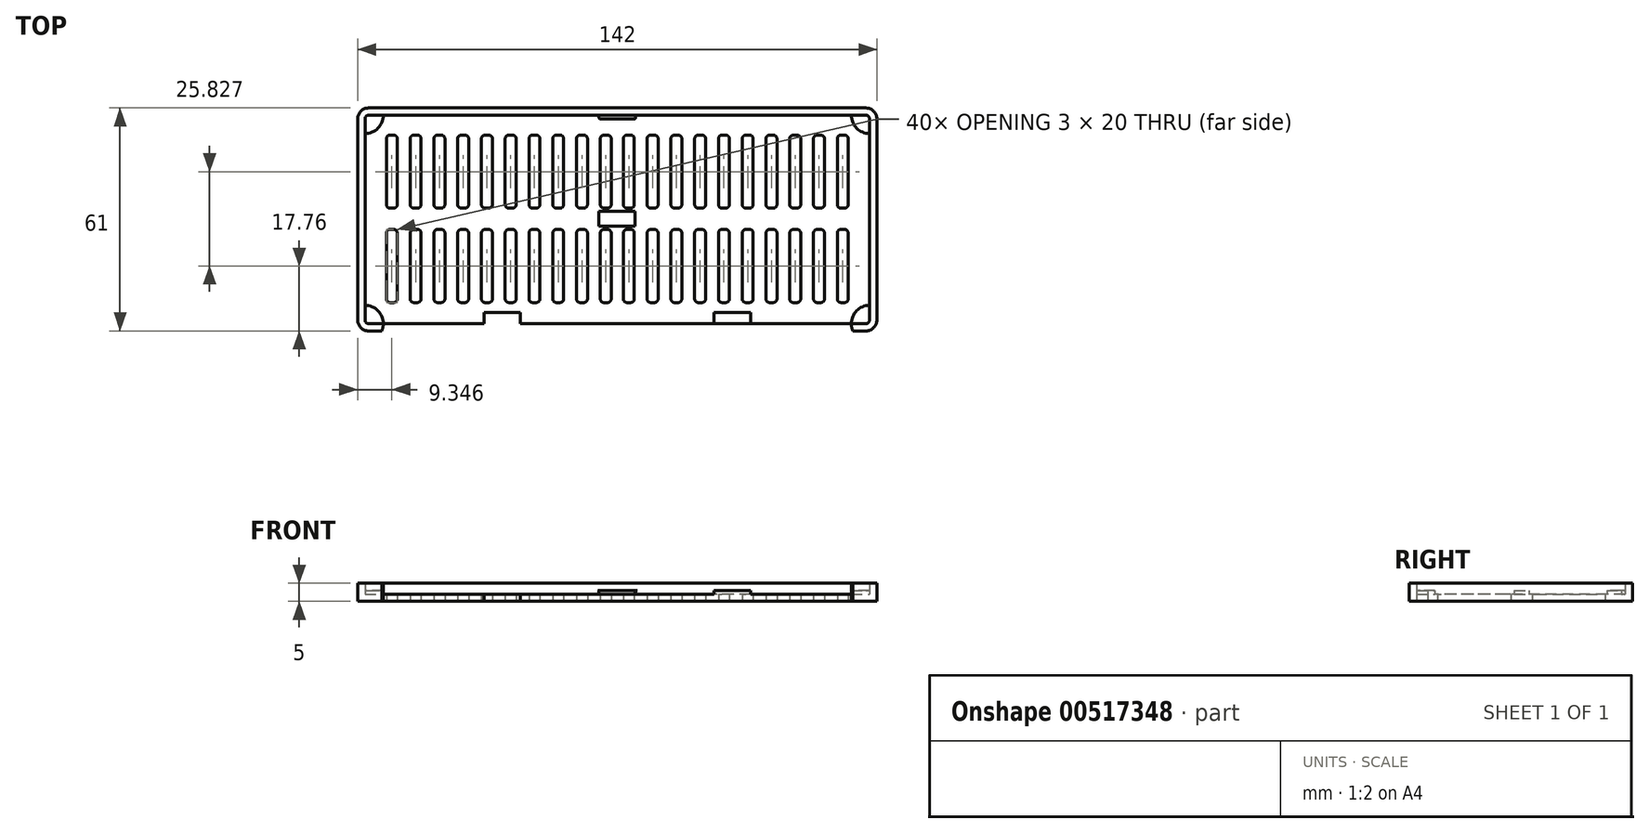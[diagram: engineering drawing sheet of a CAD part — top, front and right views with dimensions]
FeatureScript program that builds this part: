
annotation { "Feature Type Name" : "Feature", "Feature Type Description" : "" }
export const myFeature = defineFeature(function(context is Context, id is Id, definition is map)
    precondition{}
    {
        {
            var Q0;
            Q0=qCreatedBy(makeId("Top.planeOp"),FACE);
            var sketch = newSketch(context, id + "F0", { "sketchPlane" : qUnion([Q0])});
            skLineSegment(sketch, "E0.top", {"start": v(1, -57) * mm, "end": v(137, -57) * mm});
            skLineSegment(sketch, "E0.left", {"start": v(0, -1) * mm, "end": v(0, -56) * mm});
            skLineSegment(sketch, "E0.right", {"start": v(138, -1) * mm, "end": v(138, -56) * mm});
            skPoint(sketch, "E1.visualSharp", {"position": v(0, 0) * mm});
            skArc(sketch, "E1.filletArc", {"start": v(1, 0) * mm, "mid": v(0.3, -0.3) * mm, "end": v(0, -1) * mm});
            skPoint(sketch, "E2.visualSharp", {"position": v(0, -57) * mm});
            skArc(sketch, "E2.filletArc", {"start": v(0, -56) * mm, "mid": v(0.3, -56.7) * mm, "end": v(1, -57) * mm});
            skPoint(sketch, "E3.visualSharp", {"position": v(138, -57) * mm});
            skArc(sketch, "E3.filletArc", {"start": v(137, -57) * mm, "mid": v(137.7, -56.7) * mm, "end": v(138, -56) * mm});
            skPoint(sketch, "E4.visualSharp", {"position": v(138, 0) * mm});
            skArc(sketch, "E4.filletArc", {"start": v(138, -1) * mm, "mid": v(137.7, -0.3) * mm, "end": v(137, 0) * mm});
            skArc(sketch, "E5.0", {"start": v(1, 2) * mm, "mid": v(-1.12, 1.12) * mm, "end": v(-2, -1) * mm});
            skLineSegment(sketch, "E5.1", {"start": v(-2, -1) * mm, "end": v(-2, -56) * mm});
            skLineSegment(sketch, "E5.2", {"start": v(1, 2) * mm, "end": v(137, 2) * mm});
            skArc(sketch, "E5.3", {"start": v(-2, -56) * mm, "mid": v(-1.12, -58.12) * mm, "end": v(1, -59) * mm});
            skArc(sketch, "E5.4", {"start": v(140, -1) * mm, "mid": v(139.12, 1.12) * mm, "end": v(137, 2) * mm});
            skLineSegment(sketch, "E5.5", {"start": v(140, -1) * mm, "end": v(140, -56) * mm});
            skArc(sketch, "E5.6", {"start": v(137, -59) * mm, "mid": v(139.12, -58.12) * mm, "end": v(140, -56) * mm});
            skLineSegment(sketch, "E5.7", {"start": v(1, -59) * mm, "end": v(137, -59) * mm});
            skCircle(sketch, "E6", {"center": v(0, 0) * mm, "radius": 5 * mm});
            skCircle(sketch, "E7", {"center": v(0, -57) * mm, "radius": 5 * mm});
            skCircle(sketch, "E8", {"center": v(138, -57) * mm, "radius": 5 * mm});
            skCircle(sketch, "E9", {"center": v(138, 0) * mm, "radius": 5 * mm});
            skLineSegment(sketch, "E10.top", {"start": v(69, -1) * mm, "end": v(73.64, -1) * mm});
            skLineSegment(sketch, "E10.left", {"start": v(69, 0) * mm, "end": v(69, -1) * mm, "construction": true});
            skLineSegment(sketch, "E10.right", {"start": v(74, -0.43) * mm, "end": v(74, -0.64) * mm});
            skLineSegment(sketch, "E11.MirrorCS", {"start": v(69, -1) * mm, "end": v(64.36, -1) * mm});
            skLineSegment(sketch, "E12.MirrorCS", {"start": v(64, -0.36) * mm, "end": v(64, -0.64) * mm});
            skLineSegment(sketch, "E13.bottom", {"start": v(32.53, -57) * mm, "end": v(42.53, -57) * mm});
            skLineSegment(sketch, "E13.top", {"start": v(32.53, -54) * mm, "end": v(42.53, -54) * mm});
            skLineSegment(sketch, "E13.left", {"start": v(32.53, -57) * mm, "end": v(32.53, -54) * mm});
            skLineSegment(sketch, "E13.right", {"start": v(42.53, -57) * mm, "end": v(42.53, -54) * mm});
            skLineSegment(sketch, "E14.MirrorCS", {"start": v(95.47, -57) * mm, "end": v(95.47, -54) * mm});
            skLineSegment(sketch, "E15.MirrorCS", {"start": v(105.47, -54) * mm, "end": v(95.47, -54) * mm});
            skLineSegment(sketch, "E16.MirrorCS", {"start": v(105.47, -57) * mm, "end": v(105.47, -54) * mm});
            skLineSegment(sketch, "E17", {"start": v(0, -28.5) * mm, "end": v(138, -28.5) * mm, "construction": true});
            skLineSegment(sketch, "E18.top", {"start": v(6.85, -5.41) * mm, "end": v(7.85, -5.41) * mm});
            skLineSegment(sketch, "E18.left", {"start": v(5.85, -24.41) * mm, "end": v(5.85, -6.41) * mm});
            skLineSegment(sketch, "E18.right", {"start": v(8.85, -24.41) * mm, "end": v(8.85, -6.41) * mm});
            skPoint(sketch, "E19.visualSharp", {"position": v(5.85, -5.41) * mm});
            skArc(sketch, "E19.filletArc", {"start": v(6.85, -5.41) * mm, "mid": v(6.14, -5.7) * mm, "end": v(5.85, -6.41) * mm});
            skPoint(sketch, "E20.visualSharp", {"position": v(8.85, -5.41) * mm});
            skArc(sketch, "E20.filletArc", {"start": v(8.85, -6.41) * mm, "mid": v(8.55, -5.7) * mm, "end": v(7.85, -5.41) * mm});
            skLineSegment(sketch, "E21.MirrorCS", {"start": v(-0.23, -28.33) * mm, "end": v(138, -28.33) * mm, "construction": true});
            skLineSegment(sketch, "E22.bottom", {"start": v(6.85, -25.41) * mm, "end": v(7.85, -25.41) * mm});
            skArc(sketch, "E23.filletArc", {"start": v(7.85, -25.41) * mm, "mid": v(8.55, -25.12) * mm, "end": v(8.85, -24.41) * mm});
            skArc(sketch, "E24.filletArc", {"start": v(5.85, -24.41) * mm, "mid": v(6.14, -25.12) * mm, "end": v(6.85, -25.41) * mm});
            skArc(sketch, "E25.MirrorCS", {"start": v(8.85, -50.24) * mm, "mid": v(8.55, -50.95) * mm, "end": v(7.85, -51.24) * mm});
            skArc(sketch, "E26.MirrorCS", {"start": v(6.85, -51.24) * mm, "mid": v(6.14, -50.95) * mm, "end": v(5.85, -50.24) * mm});
            skLineSegment(sketch, "E27.MirrorCS", {"start": v(6.85, -51.24) * mm, "end": v(7.85, -51.24) * mm});
            skLineSegment(sketch, "E28.MirrorCS", {"start": v(8.85, -32.24) * mm, "end": v(8.85, -50.24) * mm});
            skLineSegment(sketch, "E29.MirrorCS", {"start": v(6.85, -31.24) * mm, "end": v(7.85, -31.24) * mm});
            skLineSegment(sketch, "E30.MirrorCS", {"start": v(5.85, -32.24) * mm, "end": v(5.85, -50.24) * mm});
            skArc(sketch, "E31.MirrorCS", {"start": v(5.85, -32.24) * mm, "mid": v(6.14, -31.53) * mm, "end": v(6.85, -31.24) * mm});
            skArc(sketch, "E32.MirrorCS", {"start": v(7.85, -31.24) * mm, "mid": v(8.55, -31.53) * mm, "end": v(8.85, -32.24) * mm});
            skPoint(sketch, "E33.1.0.0", {"position": v(15.35, -5.41) * mm});
            skPoint(sketch, "E33.1.0.1", {"position": v(12.35, -5.41) * mm});
            skLineSegment(sketch, "E33.1.0.2", {"start": v(15.35, -24.41) * mm, "end": v(15.35, -6.41) * mm});
            skLineSegment(sketch, "E33.1.0.3", {"start": v(12.35, -24.41) * mm, "end": v(12.35, -6.41) * mm});
            skArc(sketch, "E33.1.0.4", {"start": v(12.35, -24.41) * mm, "mid": v(12.64, -25.12) * mm, "end": v(13.35, -25.41) * mm});
            skArc(sketch, "E33.1.0.5", {"start": v(15.35, -6.41) * mm, "mid": v(15.05, -5.7) * mm, "end": v(14.35, -5.41) * mm});
            skArc(sketch, "E33.1.0.6", {"start": v(13.35, -5.41) * mm, "mid": v(12.64, -5.7) * mm, "end": v(12.35, -6.41) * mm});
            skLineSegment(sketch, "E33.1.0.7", {"start": v(13.35, -25.41) * mm, "end": v(14.35, -25.41) * mm});
            skLineSegment(sketch, "E33.1.0.8", {"start": v(13.35, -5.41) * mm, "end": v(14.35, -5.41) * mm});
            skArc(sketch, "E33.1.0.9", {"start": v(14.35, -25.41) * mm, "mid": v(15.05, -25.12) * mm, "end": v(15.35, -24.41) * mm});
            skLineSegment(sketch, "E33.1.0.10", {"start": v(15.35, -32.24) * mm, "end": v(15.35, -50.24) * mm});
            skLineSegment(sketch, "E33.1.0.11", {"start": v(12.35, -32.24) * mm, "end": v(12.35, -50.24) * mm});
            skArc(sketch, "E33.1.0.12", {"start": v(15.35, -50.24) * mm, "mid": v(15.05, -50.95) * mm, "end": v(14.35, -51.24) * mm});
            skArc(sketch, "E33.1.0.13", {"start": v(14.35, -31.24) * mm, "mid": v(15.05, -31.53) * mm, "end": v(15.35, -32.24) * mm});
            skArc(sketch, "E33.1.0.14", {"start": v(12.35, -32.24) * mm, "mid": v(12.64, -31.53) * mm, "end": v(13.35, -31.24) * mm});
            skLineSegment(sketch, "E33.1.0.15", {"start": v(13.35, -31.24) * mm, "end": v(14.35, -31.24) * mm});
            skArc(sketch, "E33.1.0.16", {"start": v(13.35, -51.24) * mm, "mid": v(12.64, -50.95) * mm, "end": v(12.35, -50.24) * mm});
            skLineSegment(sketch, "E33.1.0.17", {"start": v(13.35, -51.24) * mm, "end": v(14.35, -51.24) * mm});
            skPoint(sketch, "E33.2.0.0", {"position": v(21.85, -5.41) * mm});
            skPoint(sketch, "E33.2.0.1", {"position": v(18.85, -5.41) * mm});
            skLineSegment(sketch, "E33.2.0.2", {"start": v(21.85, -24.41) * mm, "end": v(21.85, -6.41) * mm});
            skLineSegment(sketch, "E33.2.0.3", {"start": v(18.85, -24.41) * mm, "end": v(18.85, -6.41) * mm});
            skArc(sketch, "E33.2.0.4", {"start": v(18.85, -24.41) * mm, "mid": v(19.14, -25.12) * mm, "end": v(19.85, -25.41) * mm});
            skArc(sketch, "E33.2.0.5", {"start": v(21.85, -6.41) * mm, "mid": v(21.55, -5.7) * mm, "end": v(20.85, -5.41) * mm});
            skArc(sketch, "E33.2.0.6", {"start": v(19.85, -5.41) * mm, "mid": v(19.14, -5.7) * mm, "end": v(18.85, -6.41) * mm});
            skLineSegment(sketch, "E33.2.0.7", {"start": v(19.85, -25.41) * mm, "end": v(20.85, -25.41) * mm});
            skLineSegment(sketch, "E33.2.0.8", {"start": v(19.85, -5.41) * mm, "end": v(20.85, -5.41) * mm});
            skArc(sketch, "E33.2.0.9", {"start": v(20.85, -25.41) * mm, "mid": v(21.55, -25.12) * mm, "end": v(21.85, -24.41) * mm});
            skLineSegment(sketch, "E33.2.0.10", {"start": v(21.85, -32.24) * mm, "end": v(21.85, -50.24) * mm});
            skLineSegment(sketch, "E33.2.0.11", {"start": v(18.85, -32.24) * mm, "end": v(18.85, -50.24) * mm});
            skArc(sketch, "E33.2.0.12", {"start": v(21.85, -50.24) * mm, "mid": v(21.55, -50.95) * mm, "end": v(20.85, -51.24) * mm});
            skArc(sketch, "E33.2.0.13", {"start": v(20.85, -31.24) * mm, "mid": v(21.55, -31.53) * mm, "end": v(21.85, -32.24) * mm});
            skArc(sketch, "E33.2.0.14", {"start": v(18.85, -32.24) * mm, "mid": v(19.14, -31.53) * mm, "end": v(19.85, -31.24) * mm});
            skLineSegment(sketch, "E33.2.0.15", {"start": v(19.85, -31.24) * mm, "end": v(20.85, -31.24) * mm});
            skArc(sketch, "E33.2.0.16", {"start": v(19.85, -51.24) * mm, "mid": v(19.14, -50.95) * mm, "end": v(18.85, -50.24) * mm});
            skLineSegment(sketch, "E33.2.0.17", {"start": v(19.85, -51.24) * mm, "end": v(20.85, -51.24) * mm});
            skPoint(sketch, "E33.3.0.0", {"position": v(28.35, -5.41) * mm});
            skPoint(sketch, "E33.3.0.1", {"position": v(25.35, -5.41) * mm});
            skLineSegment(sketch, "E33.3.0.2", {"start": v(28.35, -24.41) * mm, "end": v(28.35, -6.41) * mm});
            skLineSegment(sketch, "E33.3.0.3", {"start": v(25.35, -24.41) * mm, "end": v(25.35, -6.41) * mm});
            skArc(sketch, "E33.3.0.4", {"start": v(25.35, -24.41) * mm, "mid": v(25.64, -25.12) * mm, "end": v(26.35, -25.41) * mm});
            skArc(sketch, "E33.3.0.5", {"start": v(28.35, -6.41) * mm, "mid": v(28.05, -5.7) * mm, "end": v(27.35, -5.41) * mm});
            skArc(sketch, "E33.3.0.6", {"start": v(26.35, -5.41) * mm, "mid": v(25.64, -5.7) * mm, "end": v(25.35, -6.41) * mm});
            skLineSegment(sketch, "E33.3.0.7", {"start": v(26.35, -25.41) * mm, "end": v(27.35, -25.41) * mm});
            skLineSegment(sketch, "E33.3.0.8", {"start": v(26.35, -5.41) * mm, "end": v(27.35, -5.41) * mm});
            skArc(sketch, "E33.3.0.9", {"start": v(27.35, -25.41) * mm, "mid": v(28.05, -25.12) * mm, "end": v(28.35, -24.41) * mm});
            skLineSegment(sketch, "E33.3.0.10", {"start": v(28.35, -32.24) * mm, "end": v(28.35, -50.24) * mm});
            skLineSegment(sketch, "E33.3.0.11", {"start": v(25.35, -32.24) * mm, "end": v(25.35, -50.24) * mm});
            skArc(sketch, "E33.3.0.12", {"start": v(28.35, -50.24) * mm, "mid": v(28.05, -50.95) * mm, "end": v(27.35, -51.24) * mm});
            skArc(sketch, "E33.3.0.13", {"start": v(27.35, -31.24) * mm, "mid": v(28.05, -31.53) * mm, "end": v(28.35, -32.24) * mm});
            skArc(sketch, "E33.3.0.14", {"start": v(25.35, -32.24) * mm, "mid": v(25.64, -31.53) * mm, "end": v(26.35, -31.24) * mm});
            skLineSegment(sketch, "E33.3.0.15", {"start": v(26.35, -31.24) * mm, "end": v(27.35, -31.24) * mm});
            skArc(sketch, "E33.3.0.16", {"start": v(26.35, -51.24) * mm, "mid": v(25.64, -50.95) * mm, "end": v(25.35, -50.24) * mm});
            skLineSegment(sketch, "E33.3.0.17", {"start": v(26.35, -51.24) * mm, "end": v(27.35, -51.24) * mm});
            skPoint(sketch, "E33.4.0.0", {"position": v(34.85, -5.41) * mm});
            skPoint(sketch, "E33.4.0.1", {"position": v(31.85, -5.41) * mm});
            skLineSegment(sketch, "E33.4.0.2", {"start": v(34.85, -24.41) * mm, "end": v(34.85, -6.41) * mm});
            skLineSegment(sketch, "E33.4.0.3", {"start": v(31.85, -24.41) * mm, "end": v(31.85, -6.41) * mm});
            skArc(sketch, "E33.4.0.4", {"start": v(31.85, -24.41) * mm, "mid": v(32.14, -25.12) * mm, "end": v(32.85, -25.41) * mm});
            skArc(sketch, "E33.4.0.5", {"start": v(34.85, -6.41) * mm, "mid": v(34.55, -5.7) * mm, "end": v(33.85, -5.41) * mm});
            skArc(sketch, "E33.4.0.6", {"start": v(32.85, -5.41) * mm, "mid": v(32.14, -5.7) * mm, "end": v(31.85, -6.41) * mm});
            skLineSegment(sketch, "E33.4.0.7", {"start": v(32.85, -25.41) * mm, "end": v(33.85, -25.41) * mm});
            skLineSegment(sketch, "E33.4.0.8", {"start": v(32.85, -5.41) * mm, "end": v(33.85, -5.41) * mm});
            skArc(sketch, "E33.4.0.9", {"start": v(33.85, -25.41) * mm, "mid": v(34.55, -25.12) * mm, "end": v(34.85, -24.41) * mm});
            skLineSegment(sketch, "E33.4.0.10", {"start": v(34.85, -32.24) * mm, "end": v(34.85, -50.24) * mm});
            skLineSegment(sketch, "E33.4.0.11", {"start": v(31.85, -32.24) * mm, "end": v(31.85, -50.24) * mm});
            skArc(sketch, "E33.4.0.12", {"start": v(34.85, -50.24) * mm, "mid": v(34.55, -50.95) * mm, "end": v(33.85, -51.24) * mm});
            skArc(sketch, "E33.4.0.13", {"start": v(33.85, -31.24) * mm, "mid": v(34.55, -31.53) * mm, "end": v(34.85, -32.24) * mm});
            skArc(sketch, "E33.4.0.14", {"start": v(31.85, -32.24) * mm, "mid": v(32.14, -31.53) * mm, "end": v(32.85, -31.24) * mm});
            skLineSegment(sketch, "E33.4.0.15", {"start": v(32.85, -31.24) * mm, "end": v(33.85, -31.24) * mm});
            skArc(sketch, "E33.4.0.16", {"start": v(32.85, -51.24) * mm, "mid": v(32.14, -50.95) * mm, "end": v(31.85, -50.24) * mm});
            skLineSegment(sketch, "E33.4.0.17", {"start": v(32.85, -51.24) * mm, "end": v(33.85, -51.24) * mm});
            skPoint(sketch, "E33.5.0.0", {"position": v(41.35, -5.41) * mm});
            skPoint(sketch, "E33.5.0.1", {"position": v(38.35, -5.41) * mm});
            skLineSegment(sketch, "E33.5.0.2", {"start": v(41.35, -24.41) * mm, "end": v(41.35, -6.41) * mm});
            skLineSegment(sketch, "E33.5.0.3", {"start": v(38.35, -24.41) * mm, "end": v(38.35, -6.41) * mm});
            skArc(sketch, "E33.5.0.4", {"start": v(38.35, -24.41) * mm, "mid": v(38.64, -25.12) * mm, "end": v(39.35, -25.41) * mm});
            skArc(sketch, "E33.5.0.5", {"start": v(41.35, -6.41) * mm, "mid": v(41.05, -5.7) * mm, "end": v(40.35, -5.41) * mm});
            skArc(sketch, "E33.5.0.6", {"start": v(39.35, -5.41) * mm, "mid": v(38.64, -5.7) * mm, "end": v(38.35, -6.41) * mm});
            skLineSegment(sketch, "E33.5.0.7", {"start": v(39.35, -25.41) * mm, "end": v(40.35, -25.41) * mm});
            skLineSegment(sketch, "E33.5.0.8", {"start": v(39.35, -5.41) * mm, "end": v(40.35, -5.41) * mm});
            skArc(sketch, "E33.5.0.9", {"start": v(40.35, -25.41) * mm, "mid": v(41.05, -25.12) * mm, "end": v(41.35, -24.41) * mm});
            skLineSegment(sketch, "E33.5.0.10", {"start": v(41.35, -32.24) * mm, "end": v(41.35, -50.24) * mm});
            skLineSegment(sketch, "E33.5.0.11", {"start": v(38.35, -32.24) * mm, "end": v(38.35, -50.24) * mm});
            skArc(sketch, "E33.5.0.12", {"start": v(41.35, -50.24) * mm, "mid": v(41.05, -50.95) * mm, "end": v(40.35, -51.24) * mm});
            skArc(sketch, "E33.5.0.13", {"start": v(40.35, -31.24) * mm, "mid": v(41.05, -31.53) * mm, "end": v(41.35, -32.24) * mm});
            skArc(sketch, "E33.5.0.14", {"start": v(38.35, -32.24) * mm, "mid": v(38.64, -31.53) * mm, "end": v(39.35, -31.24) * mm});
            skLineSegment(sketch, "E33.5.0.15", {"start": v(39.35, -31.24) * mm, "end": v(40.35, -31.24) * mm});
            skArc(sketch, "E33.5.0.16", {"start": v(39.35, -51.24) * mm, "mid": v(38.64, -50.95) * mm, "end": v(38.35, -50.24) * mm});
            skLineSegment(sketch, "E33.5.0.17", {"start": v(39.35, -51.24) * mm, "end": v(40.35, -51.24) * mm});
            skPoint(sketch, "E33.6.0.0", {"position": v(47.85, -5.41) * mm});
            skPoint(sketch, "E33.6.0.1", {"position": v(44.85, -5.41) * mm});
            skLineSegment(sketch, "E33.6.0.2", {"start": v(47.85, -24.41) * mm, "end": v(47.85, -6.41) * mm});
            skLineSegment(sketch, "E33.6.0.3", {"start": v(44.85, -24.41) * mm, "end": v(44.85, -6.41) * mm});
            skArc(sketch, "E33.6.0.4", {"start": v(44.85, -24.41) * mm, "mid": v(45.14, -25.12) * mm, "end": v(45.85, -25.41) * mm});
            skArc(sketch, "E33.6.0.5", {"start": v(47.85, -6.41) * mm, "mid": v(47.55, -5.7) * mm, "end": v(46.85, -5.41) * mm});
            skArc(sketch, "E33.6.0.6", {"start": v(45.85, -5.41) * mm, "mid": v(45.14, -5.7) * mm, "end": v(44.85, -6.41) * mm});
            skLineSegment(sketch, "E33.6.0.7", {"start": v(45.85, -25.41) * mm, "end": v(46.85, -25.41) * mm});
            skLineSegment(sketch, "E33.6.0.8", {"start": v(45.85, -5.41) * mm, "end": v(46.85, -5.41) * mm});
            skArc(sketch, "E33.6.0.9", {"start": v(46.85, -25.41) * mm, "mid": v(47.55, -25.12) * mm, "end": v(47.85, -24.41) * mm});
            skLineSegment(sketch, "E33.6.0.10", {"start": v(47.85, -32.24) * mm, "end": v(47.85, -50.24) * mm});
            skLineSegment(sketch, "E33.6.0.11", {"start": v(44.85, -32.24) * mm, "end": v(44.85, -50.24) * mm});
            skArc(sketch, "E33.6.0.12", {"start": v(47.85, -50.24) * mm, "mid": v(47.55, -50.95) * mm, "end": v(46.85, -51.24) * mm});
            skArc(sketch, "E33.6.0.13", {"start": v(46.85, -31.24) * mm, "mid": v(47.55, -31.53) * mm, "end": v(47.85, -32.24) * mm});
            skArc(sketch, "E33.6.0.14", {"start": v(44.85, -32.24) * mm, "mid": v(45.14, -31.53) * mm, "end": v(45.85, -31.24) * mm});
            skLineSegment(sketch, "E33.6.0.15", {"start": v(45.85, -31.24) * mm, "end": v(46.85, -31.24) * mm});
            skArc(sketch, "E33.6.0.16", {"start": v(45.85, -51.24) * mm, "mid": v(45.14, -50.95) * mm, "end": v(44.85, -50.24) * mm});
            skLineSegment(sketch, "E33.6.0.17", {"start": v(45.85, -51.24) * mm, "end": v(46.85, -51.24) * mm});
            skPoint(sketch, "E33.7.0.0", {"position": v(54.35, -5.41) * mm});
            skPoint(sketch, "E33.7.0.1", {"position": v(51.35, -5.41) * mm});
            skLineSegment(sketch, "E33.7.0.2", {"start": v(54.35, -24.41) * mm, "end": v(54.35, -6.41) * mm});
            skLineSegment(sketch, "E33.7.0.3", {"start": v(51.35, -24.41) * mm, "end": v(51.35, -6.41) * mm});
            skArc(sketch, "E33.7.0.4", {"start": v(51.35, -24.41) * mm, "mid": v(51.64, -25.12) * mm, "end": v(52.35, -25.41) * mm});
            skArc(sketch, "E33.7.0.5", {"start": v(54.35, -6.41) * mm, "mid": v(54.05, -5.7) * mm, "end": v(53.35, -5.41) * mm});
            skArc(sketch, "E33.7.0.6", {"start": v(52.35, -5.41) * mm, "mid": v(51.64, -5.7) * mm, "end": v(51.35, -6.41) * mm});
            skLineSegment(sketch, "E33.7.0.7", {"start": v(52.35, -25.41) * mm, "end": v(53.35, -25.41) * mm});
            skLineSegment(sketch, "E33.7.0.8", {"start": v(52.35, -5.41) * mm, "end": v(53.35, -5.41) * mm});
            skArc(sketch, "E33.7.0.9", {"start": v(53.35, -25.41) * mm, "mid": v(54.05, -25.12) * mm, "end": v(54.35, -24.41) * mm});
            skLineSegment(sketch, "E33.7.0.10", {"start": v(54.35, -32.24) * mm, "end": v(54.35, -50.24) * mm});
            skLineSegment(sketch, "E33.7.0.11", {"start": v(51.35, -32.24) * mm, "end": v(51.35, -50.24) * mm});
            skArc(sketch, "E33.7.0.12", {"start": v(54.35, -50.24) * mm, "mid": v(54.05, -50.95) * mm, "end": v(53.35, -51.24) * mm});
            skArc(sketch, "E33.7.0.13", {"start": v(53.35, -31.24) * mm, "mid": v(54.05, -31.53) * mm, "end": v(54.35, -32.24) * mm});
            skArc(sketch, "E33.7.0.14", {"start": v(51.35, -32.24) * mm, "mid": v(51.64, -31.53) * mm, "end": v(52.35, -31.24) * mm});
            skLineSegment(sketch, "E33.7.0.15", {"start": v(52.35, -31.24) * mm, "end": v(53.35, -31.24) * mm});
            skArc(sketch, "E33.7.0.16", {"start": v(52.35, -51.24) * mm, "mid": v(51.64, -50.95) * mm, "end": v(51.35, -50.24) * mm});
            skLineSegment(sketch, "E33.7.0.17", {"start": v(52.35, -51.24) * mm, "end": v(53.35, -51.24) * mm});
            skPoint(sketch, "E33.8.0.0", {"position": v(60.85, -5.41) * mm});
            skPoint(sketch, "E33.8.0.1", {"position": v(57.85, -5.41) * mm});
            skLineSegment(sketch, "E33.8.0.2", {"start": v(60.85, -24.41) * mm, "end": v(60.85, -6.41) * mm});
            skLineSegment(sketch, "E33.8.0.3", {"start": v(57.85, -24.41) * mm, "end": v(57.85, -6.41) * mm});
            skArc(sketch, "E33.8.0.4", {"start": v(57.85, -24.41) * mm, "mid": v(58.14, -25.12) * mm, "end": v(58.85, -25.41) * mm});
            skArc(sketch, "E33.8.0.5", {"start": v(60.85, -6.41) * mm, "mid": v(60.55, -5.7) * mm, "end": v(59.85, -5.41) * mm});
            skArc(sketch, "E33.8.0.6", {"start": v(58.85, -5.41) * mm, "mid": v(58.14, -5.7) * mm, "end": v(57.85, -6.41) * mm});
            skLineSegment(sketch, "E33.8.0.7", {"start": v(58.85, -25.41) * mm, "end": v(59.85, -25.41) * mm});
            skLineSegment(sketch, "E33.8.0.8", {"start": v(58.85, -5.41) * mm, "end": v(59.85, -5.41) * mm});
            skArc(sketch, "E33.8.0.9", {"start": v(59.85, -25.41) * mm, "mid": v(60.55, -25.12) * mm, "end": v(60.85, -24.41) * mm});
            skLineSegment(sketch, "E33.8.0.10", {"start": v(60.85, -32.24) * mm, "end": v(60.85, -50.24) * mm});
            skLineSegment(sketch, "E33.8.0.11", {"start": v(57.85, -32.24) * mm, "end": v(57.85, -50.24) * mm});
            skArc(sketch, "E33.8.0.12", {"start": v(60.85, -50.24) * mm, "mid": v(60.55, -50.95) * mm, "end": v(59.85, -51.24) * mm});
            skArc(sketch, "E33.8.0.13", {"start": v(59.85, -31.24) * mm, "mid": v(60.55, -31.53) * mm, "end": v(60.85, -32.24) * mm});
            skArc(sketch, "E33.8.0.14", {"start": v(57.85, -32.24) * mm, "mid": v(58.14, -31.53) * mm, "end": v(58.85, -31.24) * mm});
            skLineSegment(sketch, "E33.8.0.15", {"start": v(58.85, -31.24) * mm, "end": v(59.85, -31.24) * mm});
            skArc(sketch, "E33.8.0.16", {"start": v(58.85, -51.24) * mm, "mid": v(58.14, -50.95) * mm, "end": v(57.85, -50.24) * mm});
            skLineSegment(sketch, "E33.8.0.17", {"start": v(58.85, -51.24) * mm, "end": v(59.85, -51.24) * mm});
            skPoint(sketch, "E33.9.0.0", {"position": v(67.35, -5.41) * mm});
            skPoint(sketch, "E33.9.0.1", {"position": v(64.35, -5.41) * mm});
            skLineSegment(sketch, "E33.9.0.2", {"start": v(67.35, -24.41) * mm, "end": v(67.35, -6.41) * mm});
            skLineSegment(sketch, "E33.9.0.3", {"start": v(64.35, -24.41) * mm, "end": v(64.35, -6.41) * mm});
            skArc(sketch, "E33.9.0.4", {"start": v(64.35, -24.41) * mm, "mid": v(64.64, -25.12) * mm, "end": v(65.35, -25.41) * mm});
            skArc(sketch, "E33.9.0.5", {"start": v(67.35, -6.41) * mm, "mid": v(67.05, -5.7) * mm, "end": v(66.35, -5.41) * mm});
            skArc(sketch, "E33.9.0.6", {"start": v(65.35, -5.41) * mm, "mid": v(64.64, -5.7) * mm, "end": v(64.35, -6.41) * mm});
            skLineSegment(sketch, "E33.9.0.7", {"start": v(65.35, -25.41) * mm, "end": v(66.35, -25.41) * mm});
            skLineSegment(sketch, "E33.9.0.8", {"start": v(65.35, -5.41) * mm, "end": v(66.35, -5.41) * mm});
            skArc(sketch, "E33.9.0.9", {"start": v(66.35, -25.41) * mm, "mid": v(67.05, -25.12) * mm, "end": v(67.35, -24.41) * mm});
            skLineSegment(sketch, "E33.9.0.10", {"start": v(67.35, -32.24) * mm, "end": v(67.35, -50.24) * mm});
            skLineSegment(sketch, "E33.9.0.11", {"start": v(64.35, -32.24) * mm, "end": v(64.35, -50.24) * mm});
            skArc(sketch, "E33.9.0.12", {"start": v(67.35, -50.24) * mm, "mid": v(67.05, -50.95) * mm, "end": v(66.35, -51.24) * mm});
            skArc(sketch, "E33.9.0.13", {"start": v(66.35, -31.24) * mm, "mid": v(67.05, -31.53) * mm, "end": v(67.35, -32.24) * mm});
            skArc(sketch, "E33.9.0.14", {"start": v(64.35, -32.24) * mm, "mid": v(64.64, -31.53) * mm, "end": v(65.35, -31.24) * mm});
            skLineSegment(sketch, "E33.9.0.15", {"start": v(65.35, -31.24) * mm, "end": v(66.35, -31.24) * mm});
            skArc(sketch, "E33.9.0.16", {"start": v(65.35, -51.24) * mm, "mid": v(64.64, -50.95) * mm, "end": v(64.35, -50.24) * mm});
            skLineSegment(sketch, "E33.9.0.17", {"start": v(65.35, -51.24) * mm, "end": v(66.35, -51.24) * mm});
            skLineSegment(sketch, "E33.direction1", {"start": v(6.85, -25.41) * mm, "end": v(13.35, -25.41) * mm, "construction": true});
            skLineSegment(sketch, "E34", {"start": v(69, -57) * mm, "end": v(69, 2) * mm, "construction": true});
            skArc(sketch, "E35.MirrorCS", {"start": v(109.65, -6.41) * mm, "mid": v(109.95, -5.7) * mm, "end": v(110.65, -5.41) * mm});
            skArc(sketch, "E36.MirrorCS", {"start": v(118.15, -5.41) * mm, "mid": v(118.86, -5.7) * mm, "end": v(119.15, -6.41) * mm});
            skLineSegment(sketch, "E37.MirrorCS", {"start": v(131.15, -5.41) * mm, "end": v(130.15, -5.41) * mm});
            skLineSegment(sketch, "E38.MirrorCS", {"start": v(111.65, -5.41) * mm, "end": v(110.65, -5.41) * mm});
            skLineSegment(sketch, "E39.MirrorCS", {"start": v(92.15, -5.41) * mm, "end": v(91.15, -5.41) * mm});
            skLineSegment(sketch, "E40.MirrorCS", {"start": v(131.15, -25.41) * mm, "end": v(130.15, -25.41) * mm});
            skLineSegment(sketch, "E41.MirrorCS", {"start": v(124.65, -25.41) * mm, "end": v(123.65, -25.41) * mm});
            skLineSegment(sketch, "E42.MirrorCS", {"start": v(98.65, -5.41) * mm, "end": v(97.65, -5.41) * mm});
            skLineSegment(sketch, "E43.MirrorCS", {"start": v(118.15, -5.41) * mm, "end": v(117.15, -5.41) * mm});
            skLineSegment(sketch, "E44.MirrorCS", {"start": v(105.15, -5.41) * mm, "end": v(104.15, -5.41) * mm});
            skArc(sketch, "E45.MirrorCS", {"start": v(77.15, -6.41) * mm, "mid": v(77.45, -5.7) * mm, "end": v(78.15, -5.41) * mm});
            skArc(sketch, "E46.MirrorCS", {"start": v(70.65, -6.41) * mm, "mid": v(70.95, -5.7) * mm, "end": v(71.65, -5.41) * mm});
            skArc(sketch, "E47.MirrorCS", {"start": v(96.65, -6.41) * mm, "mid": v(96.95, -5.7) * mm, "end": v(97.65, -5.41) * mm});
            skArc(sketch, "E48.MirrorCS", {"start": v(103.15, -6.41) * mm, "mid": v(103.45, -5.7) * mm, "end": v(104.15, -5.41) * mm});
            skArc(sketch, "E49.MirrorCS", {"start": v(90.15, -6.41) * mm, "mid": v(90.45, -5.7) * mm, "end": v(91.15, -5.41) * mm});
            skArc(sketch, "E50.MirrorCS", {"start": v(83.65, -6.41) * mm, "mid": v(83.95, -5.7) * mm, "end": v(84.65, -5.41) * mm});
            skArc(sketch, "E51.MirrorCS", {"start": v(129.15, -6.41) * mm, "mid": v(129.45, -5.7) * mm, "end": v(130.15, -5.41) * mm});
            skArc(sketch, "E52.MirrorCS", {"start": v(122.65, -6.41) * mm, "mid": v(122.95, -5.7) * mm, "end": v(123.65, -5.41) * mm});
            skArc(sketch, "E53.MirrorCS", {"start": v(116.15, -6.41) * mm, "mid": v(116.45, -5.7) * mm, "end": v(117.15, -5.41) * mm});
            skArc(sketch, "E54.MirrorCS", {"start": v(105.15, -5.41) * mm, "mid": v(105.86, -5.7) * mm, "end": v(106.15, -6.41) * mm});
            skArc(sketch, "E55.MirrorCS", {"start": v(79.15, -5.41) * mm, "mid": v(79.86, -5.7) * mm, "end": v(80.15, -6.41) * mm});
            skArc(sketch, "E56.MirrorCS", {"start": v(86.65, -24.41) * mm, "mid": v(86.36, -25.12) * mm, "end": v(85.65, -25.41) * mm});
            skArc(sketch, "E57.MirrorCS", {"start": v(124.65, -5.41) * mm, "mid": v(125.36, -5.7) * mm, "end": v(125.65, -6.41) * mm});
            skArc(sketch, "E58.MirrorCS", {"start": v(111.65, -5.41) * mm, "mid": v(112.36, -5.7) * mm, "end": v(112.65, -6.41) * mm});
            skArc(sketch, "E59.MirrorCS", {"start": v(80.15, -24.41) * mm, "mid": v(79.86, -25.12) * mm, "end": v(79.15, -25.41) * mm});
            skArc(sketch, "E60.MirrorCS", {"start": v(73.65, -24.41) * mm, "mid": v(73.36, -25.12) * mm, "end": v(72.65, -25.41) * mm});
            skArc(sketch, "E61.MirrorCS", {"start": v(72.65, -5.41) * mm, "mid": v(73.36, -5.7) * mm, "end": v(73.65, -6.41) * mm});
            skArc(sketch, "E62.MirrorCS", {"start": v(106.15, -24.41) * mm, "mid": v(105.86, -25.12) * mm, "end": v(105.15, -25.41) * mm});
            skArc(sketch, "E63.MirrorCS", {"start": v(99.65, -24.41) * mm, "mid": v(99.36, -25.12) * mm, "end": v(98.65, -25.41) * mm});
            skArc(sketch, "E64.MirrorCS", {"start": v(119.15, -24.41) * mm, "mid": v(118.86, -25.12) * mm, "end": v(118.15, -25.41) * mm});
            skArc(sketch, "E65.MirrorCS", {"start": v(93.15, -24.41) * mm, "mid": v(92.86, -25.12) * mm, "end": v(92.15, -25.41) * mm});
            skArc(sketch, "E66.MirrorCS", {"start": v(112.65, -24.41) * mm, "mid": v(112.36, -25.12) * mm, "end": v(111.65, -25.41) * mm});
            skArc(sketch, "E67.MirrorCS", {"start": v(125.65, -24.41) * mm, "mid": v(125.36, -25.12) * mm, "end": v(124.65, -25.41) * mm});
            skArc(sketch, "E68.MirrorCS", {"start": v(92.15, -5.41) * mm, "mid": v(92.86, -5.7) * mm, "end": v(93.15, -6.41) * mm});
            skArc(sketch, "E69.MirrorCS", {"start": v(98.65, -5.41) * mm, "mid": v(99.36, -5.7) * mm, "end": v(99.65, -6.41) * mm});
            skArc(sketch, "E70.MirrorCS", {"start": v(131.15, -5.41) * mm, "mid": v(131.86, -5.7) * mm, "end": v(132.15, -6.41) * mm});
            skArc(sketch, "E71.MirrorCS", {"start": v(85.65, -5.41) * mm, "mid": v(86.36, -5.7) * mm, "end": v(86.65, -6.41) * mm});
            skLineSegment(sketch, "E72.MirrorCS", {"start": v(105.15, -25.41) * mm, "end": v(104.15, -25.41) * mm});
            skArc(sketch, "E73.MirrorCS", {"start": v(130.15, -25.41) * mm, "mid": v(129.45, -25.12) * mm, "end": v(129.15, -24.41) * mm});
            skLineSegment(sketch, "E74.MirrorCS", {"start": v(79.15, -5.41) * mm, "end": v(78.15, -5.41) * mm});
            skLineSegment(sketch, "E75.MirrorCS", {"start": v(111.65, -25.41) * mm, "end": v(110.65, -25.41) * mm});
            skLineSegment(sketch, "E76.MirrorCS", {"start": v(98.65, -25.41) * mm, "end": v(97.65, -25.41) * mm});
            skArc(sketch, "E77.MirrorCS", {"start": v(110.65, -25.41) * mm, "mid": v(109.95, -25.12) * mm, "end": v(109.65, -24.41) * mm});
            skArc(sketch, "E78.MirrorCS", {"start": v(97.65, -25.41) * mm, "mid": v(96.95, -25.12) * mm, "end": v(96.65, -24.41) * mm});
            skLineSegment(sketch, "E79.MirrorCS", {"start": v(79.15, -25.41) * mm, "end": v(78.15, -25.41) * mm});
            skArc(sketch, "E80.MirrorCS", {"start": v(104.15, -25.41) * mm, "mid": v(103.45, -25.12) * mm, "end": v(103.15, -24.41) * mm});
            skArc(sketch, "E81.MirrorCS", {"start": v(132.15, -24.41) * mm, "mid": v(131.86, -25.12) * mm, "end": v(131.15, -25.41) * mm});
            skArc(sketch, "E82.MirrorCS", {"start": v(117.15, -25.41) * mm, "mid": v(116.45, -25.12) * mm, "end": v(116.15, -24.41) * mm});
            skLineSegment(sketch, "E83.MirrorCS", {"start": v(72.65, -25.41) * mm, "end": v(71.65, -25.41) * mm});
            skLineSegment(sketch, "E84.MirrorCS", {"start": v(92.15, -25.41) * mm, "end": v(91.15, -25.41) * mm});
            skLineSegment(sketch, "E85.MirrorCS", {"start": v(118.15, -25.41) * mm, "end": v(117.15, -25.41) * mm});
            skArc(sketch, "E86.MirrorCS", {"start": v(84.65, -25.41) * mm, "mid": v(83.95, -25.12) * mm, "end": v(83.65, -24.41) * mm});
            skArc(sketch, "E87.MirrorCS", {"start": v(71.65, -25.41) * mm, "mid": v(70.95, -25.12) * mm, "end": v(70.65, -24.41) * mm});
            skArc(sketch, "E88.MirrorCS", {"start": v(91.15, -25.41) * mm, "mid": v(90.45, -25.12) * mm, "end": v(90.15, -24.41) * mm});
            skArc(sketch, "E89.MirrorCS", {"start": v(78.15, -25.41) * mm, "mid": v(77.45, -25.12) * mm, "end": v(77.15, -24.41) * mm});
            skLineSegment(sketch, "E90.MirrorCS", {"start": v(72.65, -5.41) * mm, "end": v(71.65, -5.41) * mm});
            skLineSegment(sketch, "E91.MirrorCS", {"start": v(124.65, -5.41) * mm, "end": v(123.65, -5.41) * mm});
            skLineSegment(sketch, "E92.MirrorCS", {"start": v(85.65, -25.41) * mm, "end": v(84.65, -25.41) * mm});
            skLineSegment(sketch, "E93.MirrorCS", {"start": v(85.65, -5.41) * mm, "end": v(84.65, -5.41) * mm});
            skArc(sketch, "E94.MirrorCS", {"start": v(123.65, -25.41) * mm, "mid": v(122.95, -25.12) * mm, "end": v(122.65, -24.41) * mm});
            skPoint(sketch, "E95.MirrorP", {"position": v(96.65, -5.41) * mm});
            skLineSegment(sketch, "E96.MirrorCS", {"start": v(103.15, -24.41) * mm, "end": v(103.15, -6.41) * mm});
            skPoint(sketch, "E97.MirrorP", {"position": v(119.15, -5.41) * mm});
            skLineSegment(sketch, "E98.MirrorCS", {"start": v(70.65, -24.41) * mm, "end": v(70.65, -6.41) * mm});
            skLineSegment(sketch, "E99.MirrorCS", {"start": v(116.15, -24.41) * mm, "end": v(116.15, -6.41) * mm});
            skLineSegment(sketch, "E100.MirrorCS", {"start": v(96.65, -24.41) * mm, "end": v(96.65, -6.41) * mm});
            skPoint(sketch, "E101.MirrorP", {"position": v(83.65, -5.41) * mm});
            skLineSegment(sketch, "E102.MirrorCS", {"start": v(132.15, -24.41) * mm, "end": v(132.15, -6.41) * mm});
            skLineSegment(sketch, "E103.MirrorCS", {"start": v(131.15, -25.41) * mm, "end": v(124.65, -25.41) * mm, "construction": true});
            skLineSegment(sketch, "E104.MirrorCS", {"start": v(77.15, -24.41) * mm, "end": v(77.15, -6.41) * mm});
            skPoint(sketch, "E105.MirrorP", {"position": v(93.15, -5.41) * mm});
            skPoint(sketch, "E106.MirrorP", {"position": v(116.15, -5.41) * mm});
            skLineSegment(sketch, "E107.MirrorCS", {"start": v(83.65, -24.41) * mm, "end": v(83.65, -6.41) * mm});
            skPoint(sketch, "E108.MirrorP", {"position": v(77.15, -5.41) * mm});
            skPoint(sketch, "E109.MirrorP", {"position": v(129.15, -5.41) * mm});
            skPoint(sketch, "E110.MirrorP", {"position": v(109.65, -5.41) * mm});
            skPoint(sketch, "E111.MirrorP", {"position": v(80.15, -5.41) * mm});
            skLineSegment(sketch, "E112.MirrorCS", {"start": v(90.15, -24.41) * mm, "end": v(90.15, -6.41) * mm});
            skPoint(sketch, "E113.MirrorP", {"position": v(132.15, -5.41) * mm});
            skPoint(sketch, "E114.MirrorP", {"position": v(90.15, -5.41) * mm});
            skPoint(sketch, "E115.MirrorP", {"position": v(112.65, -5.41) * mm});
            skLineSegment(sketch, "E116.MirrorCS", {"start": v(112.65, -24.41) * mm, "end": v(112.65, -6.41) * mm});
            skLineSegment(sketch, "E117.MirrorCS", {"start": v(119.15, -24.41) * mm, "end": v(119.15, -6.41) * mm});
            skLineSegment(sketch, "E118.MirrorCS", {"start": v(125.65, -24.41) * mm, "end": v(125.65, -6.41) * mm});
            skPoint(sketch, "E119.MirrorP", {"position": v(99.65, -5.41) * mm});
            skLineSegment(sketch, "E120.MirrorCS", {"start": v(129.15, -24.41) * mm, "end": v(129.15, -6.41) * mm});
            skLineSegment(sketch, "E121.MirrorCS", {"start": v(86.65, -24.41) * mm, "end": v(86.65, -6.41) * mm});
            skLineSegment(sketch, "E122.MirrorCS", {"start": v(99.65, -24.41) * mm, "end": v(99.65, -6.41) * mm});
            skLineSegment(sketch, "E123.MirrorCS", {"start": v(93.15, -24.41) * mm, "end": v(93.15, -6.41) * mm});
            skLineSegment(sketch, "E124.MirrorCS", {"start": v(109.65, -24.41) * mm, "end": v(109.65, -6.41) * mm});
            skLineSegment(sketch, "E125.MirrorCS", {"start": v(106.15, -24.41) * mm, "end": v(106.15, -6.41) * mm});
            skLineSegment(sketch, "E126.MirrorCS", {"start": v(80.15, -24.41) * mm, "end": v(80.15, -6.41) * mm});
            skLineSegment(sketch, "E127.MirrorCS", {"start": v(73.65, -24.41) * mm, "end": v(73.65, -6.41) * mm});
            skLineSegment(sketch, "E128.MirrorCS", {"start": v(122.65, -24.41) * mm, "end": v(122.65, -6.41) * mm});
            skPoint(sketch, "E129.MirrorP", {"position": v(73.65, -5.41) * mm});
            skPoint(sketch, "E130.MirrorP", {"position": v(70.65, -5.41) * mm});
            skPoint(sketch, "E131.MirrorP", {"position": v(103.15, -5.41) * mm});
            skPoint(sketch, "E132.MirrorP", {"position": v(122.65, -5.41) * mm});
            skPoint(sketch, "E133.MirrorP", {"position": v(106.15, -5.41) * mm});
            skPoint(sketch, "E134.MirrorP", {"position": v(86.65, -5.41) * mm});
            skPoint(sketch, "E135.MirrorP", {"position": v(125.65, -5.41) * mm});
            skArc(sketch, "E136.MirrorCS", {"start": v(93.15, -32.24) * mm, "mid": v(92.86, -31.53) * mm, "end": v(92.15, -31.24) * mm});
            skArc(sketch, "E137.MirrorCS", {"start": v(104.15, -31.24) * mm, "mid": v(103.45, -31.53) * mm, "end": v(103.15, -32.24) * mm});
            skArc(sketch, "E138.MirrorCS", {"start": v(110.65, -31.24) * mm, "mid": v(109.95, -31.53) * mm, "end": v(109.65, -32.24) * mm});
            skLineSegment(sketch, "E139.MirrorCS", {"start": v(98.65, -51.24) * mm, "end": v(97.65, -51.24) * mm});
            skArc(sketch, "E140.MirrorCS", {"start": v(129.15, -50.24) * mm, "mid": v(129.45, -50.95) * mm, "end": v(130.15, -51.24) * mm});
            skLineSegment(sketch, "E141.MirrorCS", {"start": v(92.15, -51.24) * mm, "end": v(91.15, -51.24) * mm});
            skLineSegment(sketch, "E142.MirrorCS", {"start": v(111.65, -51.24) * mm, "end": v(110.65, -51.24) * mm});
            skArc(sketch, "E143.MirrorCS", {"start": v(97.65, -31.24) * mm, "mid": v(96.95, -31.53) * mm, "end": v(96.65, -32.24) * mm});
            skArc(sketch, "E144.MirrorCS", {"start": v(96.65, -50.24) * mm, "mid": v(96.95, -50.95) * mm, "end": v(97.65, -51.24) * mm});
            skLineSegment(sketch, "E145.MirrorCS", {"start": v(105.15, -51.24) * mm, "end": v(104.15, -51.24) * mm});
            skArc(sketch, "E146.MirrorCS", {"start": v(91.15, -31.24) * mm, "mid": v(90.45, -31.53) * mm, "end": v(90.15, -32.24) * mm});
            skArc(sketch, "E147.MirrorCS", {"start": v(109.65, -50.24) * mm, "mid": v(109.95, -50.95) * mm, "end": v(110.65, -51.24) * mm});
            skArc(sketch, "E148.MirrorCS", {"start": v(131.15, -51.24) * mm, "mid": v(131.86, -50.95) * mm, "end": v(132.15, -50.24) * mm});
            skArc(sketch, "E149.MirrorCS", {"start": v(125.65, -32.24) * mm, "mid": v(125.36, -31.53) * mm, "end": v(124.65, -31.24) * mm});
            skArc(sketch, "E150.MirrorCS", {"start": v(116.15, -50.24) * mm, "mid": v(116.45, -50.95) * mm, "end": v(117.15, -51.24) * mm});
            skArc(sketch, "E151.MirrorCS", {"start": v(123.65, -31.24) * mm, "mid": v(122.95, -31.53) * mm, "end": v(122.65, -32.24) * mm});
            skArc(sketch, "E152.MirrorCS", {"start": v(84.65, -31.24) * mm, "mid": v(83.95, -31.53) * mm, "end": v(83.65, -32.24) * mm});
            skArc(sketch, "E153.MirrorCS", {"start": v(71.65, -31.24) * mm, "mid": v(70.95, -31.53) * mm, "end": v(70.65, -32.24) * mm});
            skLineSegment(sketch, "E154.MirrorCS", {"start": v(131.15, -51.24) * mm, "end": v(130.15, -51.24) * mm});
            skArc(sketch, "E155.MirrorCS", {"start": v(117.15, -31.24) * mm, "mid": v(116.45, -31.53) * mm, "end": v(116.15, -32.24) * mm});
            skArc(sketch, "E156.MirrorCS", {"start": v(103.15, -50.24) * mm, "mid": v(103.45, -50.95) * mm, "end": v(104.15, -51.24) * mm});
            skArc(sketch, "E157.MirrorCS", {"start": v(122.65, -50.24) * mm, "mid": v(122.95, -50.95) * mm, "end": v(123.65, -51.24) * mm});
            skArc(sketch, "E158.MirrorCS", {"start": v(119.15, -32.24) * mm, "mid": v(118.86, -31.53) * mm, "end": v(118.15, -31.24) * mm});
            skArc(sketch, "E159.MirrorCS", {"start": v(106.15, -32.24) * mm, "mid": v(105.86, -31.53) * mm, "end": v(105.15, -31.24) * mm});
            skArc(sketch, "E160.MirrorCS", {"start": v(99.65, -32.24) * mm, "mid": v(99.36, -31.53) * mm, "end": v(98.65, -31.24) * mm});
            skArc(sketch, "E161.MirrorCS", {"start": v(70.65, -50.24) * mm, "mid": v(70.95, -50.95) * mm, "end": v(71.65, -51.24) * mm});
            skArc(sketch, "E162.MirrorCS", {"start": v(83.65, -50.24) * mm, "mid": v(83.95, -50.95) * mm, "end": v(84.65, -51.24) * mm});
            skArc(sketch, "E163.MirrorCS", {"start": v(77.15, -50.24) * mm, "mid": v(77.45, -50.95) * mm, "end": v(78.15, -51.24) * mm});
            skArc(sketch, "E164.MirrorCS", {"start": v(78.15, -31.24) * mm, "mid": v(77.45, -31.53) * mm, "end": v(77.15, -32.24) * mm});
            skArc(sketch, "E165.MirrorCS", {"start": v(73.65, -32.24) * mm, "mid": v(73.36, -31.53) * mm, "end": v(72.65, -31.24) * mm});
            skArc(sketch, "E166.MirrorCS", {"start": v(90.15, -50.24) * mm, "mid": v(90.45, -50.95) * mm, "end": v(91.15, -51.24) * mm});
            skArc(sketch, "E167.MirrorCS", {"start": v(112.65, -32.24) * mm, "mid": v(112.36, -31.53) * mm, "end": v(111.65, -31.24) * mm});
            skLineSegment(sketch, "E168.MirrorCS", {"start": v(131.15, -31.24) * mm, "end": v(130.15, -31.24) * mm});
            skLineSegment(sketch, "E169.MirrorCS", {"start": v(79.15, -51.24) * mm, "end": v(78.15, -51.24) * mm});
            skArc(sketch, "E170.MirrorCS", {"start": v(118.15, -51.24) * mm, "mid": v(118.86, -50.95) * mm, "end": v(119.15, -50.24) * mm});
            skLineSegment(sketch, "E171.MirrorCS", {"start": v(124.65, -31.24) * mm, "end": v(123.65, -31.24) * mm});
            skLineSegment(sketch, "E172.MirrorCS", {"start": v(98.65, -31.24) * mm, "end": v(97.65, -31.24) * mm});
            skLineSegment(sketch, "E173.MirrorCS", {"start": v(118.15, -51.24) * mm, "end": v(117.15, -51.24) * mm});
            skLineSegment(sketch, "E174.MirrorCS", {"start": v(92.15, -31.24) * mm, "end": v(91.15, -31.24) * mm});
            skArc(sketch, "E175.MirrorCS", {"start": v(86.65, -32.24) * mm, "mid": v(86.36, -31.53) * mm, "end": v(85.65, -31.24) * mm});
            skLineSegment(sketch, "E176.MirrorCS", {"start": v(105.15, -31.24) * mm, "end": v(104.15, -31.24) * mm});
            skArc(sketch, "E177.MirrorCS", {"start": v(132.15, -32.24) * mm, "mid": v(131.86, -31.53) * mm, "end": v(131.15, -31.24) * mm});
            skArc(sketch, "E178.MirrorCS", {"start": v(124.65, -51.24) * mm, "mid": v(125.36, -50.95) * mm, "end": v(125.65, -50.24) * mm});
            skLineSegment(sketch, "E179.MirrorCS", {"start": v(85.65, -31.24) * mm, "end": v(84.65, -31.24) * mm});
            skArc(sketch, "E180.MirrorCS", {"start": v(72.65, -51.24) * mm, "mid": v(73.36, -50.95) * mm, "end": v(73.65, -50.24) * mm});
            skArc(sketch, "E181.MirrorCS", {"start": v(130.15, -31.24) * mm, "mid": v(129.45, -31.53) * mm, "end": v(129.15, -32.24) * mm});
            skLineSegment(sketch, "E182.MirrorCS", {"start": v(79.15, -31.24) * mm, "end": v(78.15, -31.24) * mm});
            skArc(sketch, "E183.MirrorCS", {"start": v(111.65, -51.24) * mm, "mid": v(112.36, -50.95) * mm, "end": v(112.65, -50.24) * mm});
            skLineSegment(sketch, "E184.MirrorCS", {"start": v(72.65, -31.24) * mm, "end": v(71.65, -31.24) * mm});
            skLineSegment(sketch, "E185.MirrorCS", {"start": v(124.65, -51.24) * mm, "end": v(123.65, -51.24) * mm});
            skLineSegment(sketch, "E186.MirrorCS", {"start": v(72.65, -51.24) * mm, "end": v(71.65, -51.24) * mm});
            skLineSegment(sketch, "E187.MirrorCS", {"start": v(118.15, -31.24) * mm, "end": v(117.15, -31.24) * mm});
            skArc(sketch, "E188.MirrorCS", {"start": v(85.65, -51.24) * mm, "mid": v(86.36, -50.95) * mm, "end": v(86.65, -50.24) * mm});
            skArc(sketch, "E189.MirrorCS", {"start": v(92.15, -51.24) * mm, "mid": v(92.86, -50.95) * mm, "end": v(93.15, -50.24) * mm});
            skArc(sketch, "E190.MirrorCS", {"start": v(80.15, -32.24) * mm, "mid": v(79.86, -31.53) * mm, "end": v(79.15, -31.24) * mm});
            skLineSegment(sketch, "E191.MirrorCS", {"start": v(111.65, -31.24) * mm, "end": v(110.65, -31.24) * mm});
            skArc(sketch, "E192.MirrorCS", {"start": v(98.65, -51.24) * mm, "mid": v(99.36, -50.95) * mm, "end": v(99.65, -50.24) * mm});
            skArc(sketch, "E193.MirrorCS", {"start": v(105.15, -51.24) * mm, "mid": v(105.86, -50.95) * mm, "end": v(106.15, -50.24) * mm});
            skLineSegment(sketch, "E194.MirrorCS", {"start": v(85.65, -51.24) * mm, "end": v(84.65, -51.24) * mm});
            skArc(sketch, "E195.MirrorCS", {"start": v(79.15, -51.24) * mm, "mid": v(79.86, -50.95) * mm, "end": v(80.15, -50.24) * mm});
            skLineSegment(sketch, "E196.MirrorCS", {"start": v(90.15, -32.24) * mm, "end": v(90.15, -50.24) * mm});
            skLineSegment(sketch, "E197.MirrorCS", {"start": v(112.65, -32.24) * mm, "end": v(112.65, -50.24) * mm});
            skLineSegment(sketch, "E198.MirrorCS", {"start": v(129.15, -32.24) * mm, "end": v(129.15, -50.24) * mm});
            skLineSegment(sketch, "E199.MirrorCS", {"start": v(125.65, -32.24) * mm, "end": v(125.65, -50.24) * mm});
            skLineSegment(sketch, "E200.MirrorCS", {"start": v(122.65, -32.24) * mm, "end": v(122.65, -50.24) * mm});
            skLineSegment(sketch, "E201.MirrorCS", {"start": v(86.65, -32.24) * mm, "end": v(86.65, -50.24) * mm});
            skLineSegment(sketch, "E202.MirrorCS", {"start": v(99.65, -32.24) * mm, "end": v(99.65, -50.24) * mm});
            skLineSegment(sketch, "E203.MirrorCS", {"start": v(119.15, -32.24) * mm, "end": v(119.15, -50.24) * mm});
            skLineSegment(sketch, "E204.MirrorCS", {"start": v(73.65, -32.24) * mm, "end": v(73.65, -50.24) * mm});
            skLineSegment(sketch, "E205.MirrorCS", {"start": v(80.15, -32.24) * mm, "end": v(80.15, -50.24) * mm});
            skLineSegment(sketch, "E206.MirrorCS", {"start": v(93.15, -32.24) * mm, "end": v(93.15, -50.24) * mm});
            skLineSegment(sketch, "E207.MirrorCS", {"start": v(106.15, -32.24) * mm, "end": v(106.15, -50.24) * mm});
            skLineSegment(sketch, "E208.MirrorCS", {"start": v(96.65, -32.24) * mm, "end": v(96.65, -50.24) * mm});
            skLineSegment(sketch, "E209.MirrorCS", {"start": v(103.15, -32.24) * mm, "end": v(103.15, -50.24) * mm});
            skLineSegment(sketch, "E210.MirrorCS", {"start": v(109.65, -32.24) * mm, "end": v(109.65, -50.24) * mm});
            skLineSegment(sketch, "E211.MirrorCS", {"start": v(116.15, -32.24) * mm, "end": v(116.15, -50.24) * mm});
            skLineSegment(sketch, "E212.MirrorCS", {"start": v(83.65, -32.24) * mm, "end": v(83.65, -50.24) * mm});
            skLineSegment(sketch, "E213.MirrorCS", {"start": v(70.65, -32.24) * mm, "end": v(70.65, -50.24) * mm});
            skLineSegment(sketch, "E214.MirrorCS", {"start": v(77.15, -32.24) * mm, "end": v(77.15, -50.24) * mm});
            skLineSegment(sketch, "E215.MirrorCS", {"start": v(132.15, -32.24) * mm, "end": v(132.15, -50.24) * mm});
            skLineSegment(sketch, "E216", {"start": v(1, 0) * mm, "end": v(63.64, 0) * mm});
            skLineSegment(sketch, "E217", {"start": v(74.43, 0) * mm, "end": v(137, 0) * mm});
            skLineSegment(sketch, "E218.bottom", {"start": v(73.88, -30.33) * mm, "end": v(63.88, -30.33) * mm});
            skLineSegment(sketch, "E218.top", {"start": v(73.88, -26.33) * mm, "end": v(63.88, -26.33) * mm});
            skLineSegment(sketch, "E218.left", {"start": v(73.88, -30.33) * mm, "end": v(73.88, -26.33) * mm});
            skLineSegment(sketch, "E218.right", {"start": v(63.88, -30.33) * mm, "end": v(63.88, -26.33) * mm});
            skPoint(sketch, "E218.middle", {"position": v(68.88, -28.33) * mm});
            skPoint(sketch, "E219.visualSharp", {"position": v(74, 0) * mm});
            skArc(sketch, "E219.filletArc", {"start": v(74.43, 0) * mm, "mid": v(74.13, -0.13) * mm, "end": v(74, -0.43) * mm});
            skPoint(sketch, "E220.visualSharp", {"position": v(74, -1) * mm});
            skArc(sketch, "E220.filletArc", {"start": v(73.64, -1) * mm, "mid": v(73.9, -0.9) * mm, "end": v(74, -0.64) * mm});
            skPoint(sketch, "E221.visualSharp", {"position": v(64, -1) * mm});
            skArc(sketch, "E221.filletArc", {"start": v(64, -0.64) * mm, "mid": v(64.1, -0.9) * mm, "end": v(64.36, -1) * mm});
            skPoint(sketch, "E222.visualSharp", {"position": v(64, 0) * mm});
            skArc(sketch, "E222.filletArc", {"start": v(64, -0.36) * mm, "mid": v(63.9, -0.1) * mm, "end": v(63.64, 0) * mm});
            skLineSegment(sketch, "E223", {"start": v(63.64, 0) * mm, "end": v(74.43, 0) * mm});
            skSolve(sketch);
        }
        {
            var Q0;
            Q0=makeQuery(id+"F0.imprint","IMPRINT",FACE,{"disambiguationData":[TD([[makeQuery(id+"F0.imprint","IMPRINT",EDGE,{"derivedFrom":sQuery(id+"F0.wireOp",EDGE,"E10.top")}),-1.0]])]});
            var Q1;
            {var subQ1=sQuery(id+"F0.wireOp",EDGE,"E22.top");Q1=makeQuery(id+"F0.imprint","IMPRINT",FACE,{"disambiguationData":[TD([[makeQuery(id+"F0.imprint","IMPRINT",EDGE,{"derivedFrom":subQ1}),-1.0]])]});}
            extrude(context, id + "F1", {"entities" : qUnion([Q0, Q1]), "depth" : 2 * mm, "offsetDistance" : 25 * mm});
        }
        {
            var Q0;
            {var subQ0=sQuery(id+"F0.wireOp",EDGE,"E1.filletArc");Q0=makeQuery(id+"F0.imprint","IMPRINT",FACE,{"disambiguationData":[TD([[makeQuery(id+"F0.imprint","IMPRINT",EDGE,{"derivedFrom":subQ0}),1.0]])]});}
            var Q1;
            {var subQ0=sQuery(id+"F0.wireOp",EDGE,"E2.filletArc");Q1=makeQuery(id+"F0.imprint","IMPRINT",FACE,{"disambiguationData":[TD([[makeQuery(id+"F0.imprint","IMPRINT",EDGE,{"derivedFrom":subQ0}),1.0]])]});}
            var Q2;
            Q2=makeQuery(id+"F0.imprint","IMPRINT",FACE,{"disambiguationData":[TD([[makeQuery(id+"F0.imprint","IMPRINT",EDGE,{"derivedFrom":sQuery(id+"F0.wireOp",EDGE,"E13.bottom")}),1.0]])]});
            var Q3;
            Q3=makeQuery(id+"F0.imprint","IMPRINT",FACE,{"disambiguationData":[TD([[makeQuery(id+"F0.imprint","IMPRINT",EDGE,{"derivedFrom":sQuery(id+"F0.wireOp",EDGE,"E218.bottom")}),-1.0]])]});
            var Q4;
            {var subQ0=sQuery(id+"F0.wireOp",EDGE,"E14.MirrorCS");Q4=makeQuery(id+"F0.imprint","IMPRINT",FACE,{"disambiguationData":[TD([[makeQuery(id+"F0.imprint","IMPRINT",EDGE,{"derivedFrom":subQ0}),-1.0]])]});}
            var Q5;
            {var subQ0=sQuery(id+"F0.wireOp",EDGE,"E3.filletArc");Q5=makeQuery(id+"F0.imprint","IMPRINT",FACE,{"disambiguationData":[TD([[makeQuery(id+"F0.imprint","IMPRINT",EDGE,{"derivedFrom":subQ0}),1.0]])]});}
            var Q6;
            {var subQ0=sQuery(id+"F0.wireOp",EDGE,"E4.filletArc");Q6=makeQuery(id+"F0.imprint","IMPRINT",FACE,{"disambiguationData":[TD([[makeQuery(id+"F0.imprint","IMPRINT",EDGE,{"derivedFrom":subQ0}),1.0]])]});}
            var Q7;
            Q7=makeQuery(id+"F0.imprint","IMPRINT",FACE,{"disambiguationData":[TD([[makeQuery(id+"F0.imprint","IMPRINT",EDGE,{"derivedFrom":sQuery(id+"F0.wireOp",EDGE,"E10.top")}),1.0]])]});
            extrude(context, id + "F2", {"entities" : qUnion([Q0, Q1, Q2, Q3, Q4, Q5, Q6, Q7]), "operationType" : NewBodyOperationType.ADD, "depth" : 3 * mm, "offsetDistance" : 25 * mm});
        }
        {
            var Q0;
            {var subQ0=sQuery(id+"F0.wireOp",EDGE,"E0.bottom");var subQ4=makeQuery(id+"F0.imprint","INTERSECT",VERTEX,{"derivedFrom":[subQ0,sQuery(id+"F0.wireOp",EDGE,"E12.MirrorCS")]});Q0=makeQuery(id+"F0.imprint","IMPRINT",FACE,{"disambiguationData":[TD([[makeQuery(id+"F0.imprint","IMPRINT",EDGE,{"disambiguationData":[TD([[subQ4,1.0]])],"derivedFrom":subQ0}),1.0]])]});}
            var Q1;
            {var subQ0=sQuery(id+"F0.wireOp",EDGE,"E9");var subQ1=sQuery(id+"F0.wireOp",EDGE,"E0.right");var subQ2=makeQuery(id+"F0.imprint","INTERSECT",VERTEX,{"derivedFrom":[subQ1,subQ0]});Q1=makeQuery(id+"F0.imprint","IMPRINT",FACE,{"disambiguationData":[TD([[makeQuery(id+"F0.imprint","IMPRINT",EDGE,{"disambiguationData":[TD([[subQ2,-1.0]])],"derivedFrom":subQ1}),1.0]])]});}
            var Q2;
            {var subQ6=sQuery(id+"F0.wireOp",EDGE,"E4.filletArc");Q2=makeQuery(id+"F0.imprint","IMPRINT",FACE,{"disambiguationData":[TD([[makeQuery(id+"F0.imprint","IMPRINT",EDGE,{"derivedFrom":subQ6}),-1.0]])]});}
            var Q3;
            {var subQ4=sQuery(id+"F0.wireOp",EDGE,"E3.filletArc");Q3=makeQuery(id+"F0.imprint","IMPRINT",FACE,{"disambiguationData":[TD([[makeQuery(id+"F0.imprint","IMPRINT",EDGE,{"derivedFrom":subQ4}),-1.0]])]});}
            var Q4;
            {var subQ5=sQuery(id+"F0.wireOp",EDGE,"E13.bottom");Q4=makeQuery(id+"F0.imprint","IMPRINT",FACE,{"disambiguationData":[TD([[makeQuery(id+"F0.imprint","IMPRINT",EDGE,{"derivedFrom":subQ5}),-1.0]])]});}
            var Q5;
            {var subQ4=sQuery(id+"F0.wireOp",EDGE,"E2.filletArc");Q5=makeQuery(id+"F0.imprint","IMPRINT",FACE,{"disambiguationData":[TD([[makeQuery(id+"F0.imprint","IMPRINT",EDGE,{"derivedFrom":subQ4}),-1.0]])]});}
            var Q6;
            {var subQ0=sQuery(id+"F0.wireOp",EDGE,"E6");var subQ1=sQuery(id+"F0.wireOp",EDGE,"E0.left");var subQ2=makeQuery(id+"F0.imprint","INTERSECT",VERTEX,{"derivedFrom":[subQ1,subQ0]});Q6=makeQuery(id+"F0.imprint","IMPRINT",FACE,{"disambiguationData":[TD([[makeQuery(id+"F0.imprint","IMPRINT",EDGE,{"disambiguationData":[TD([[subQ2,-1.0]])],"derivedFrom":subQ1}),-1.0]])]});}
            var Q7;
            {var subQ0=sQuery(id+"F0.wireOp",EDGE,"E1.filletArc");Q7=makeQuery(id+"F0.imprint","IMPRINT",FACE,{"disambiguationData":[TD([[makeQuery(id+"F0.imprint","IMPRINT",EDGE,{"derivedFrom":subQ0}),-1.0]])]});}
            var Q8;
            {var subQ0=sQuery(id+"F0.wireOp",EDGE,"E223");Q8=makeQuery(id+"F0.imprint","IMPRINT",FACE,{"disambiguationData":[TD([[makeQuery(id+"F0.imprint","IMPRINT",EDGE,{"derivedFrom":subQ0}),1.0]])]});}
            extrude(context, id + "F3", {"entities" : qUnion([Q0, Q1, Q2, Q3, Q4, Q5, Q6, Q7, Q8]), "operationType" : NewBodyOperationType.ADD, "depth" : 5 * mm, "offsetDistance" : 25 * mm});
        }
    });
